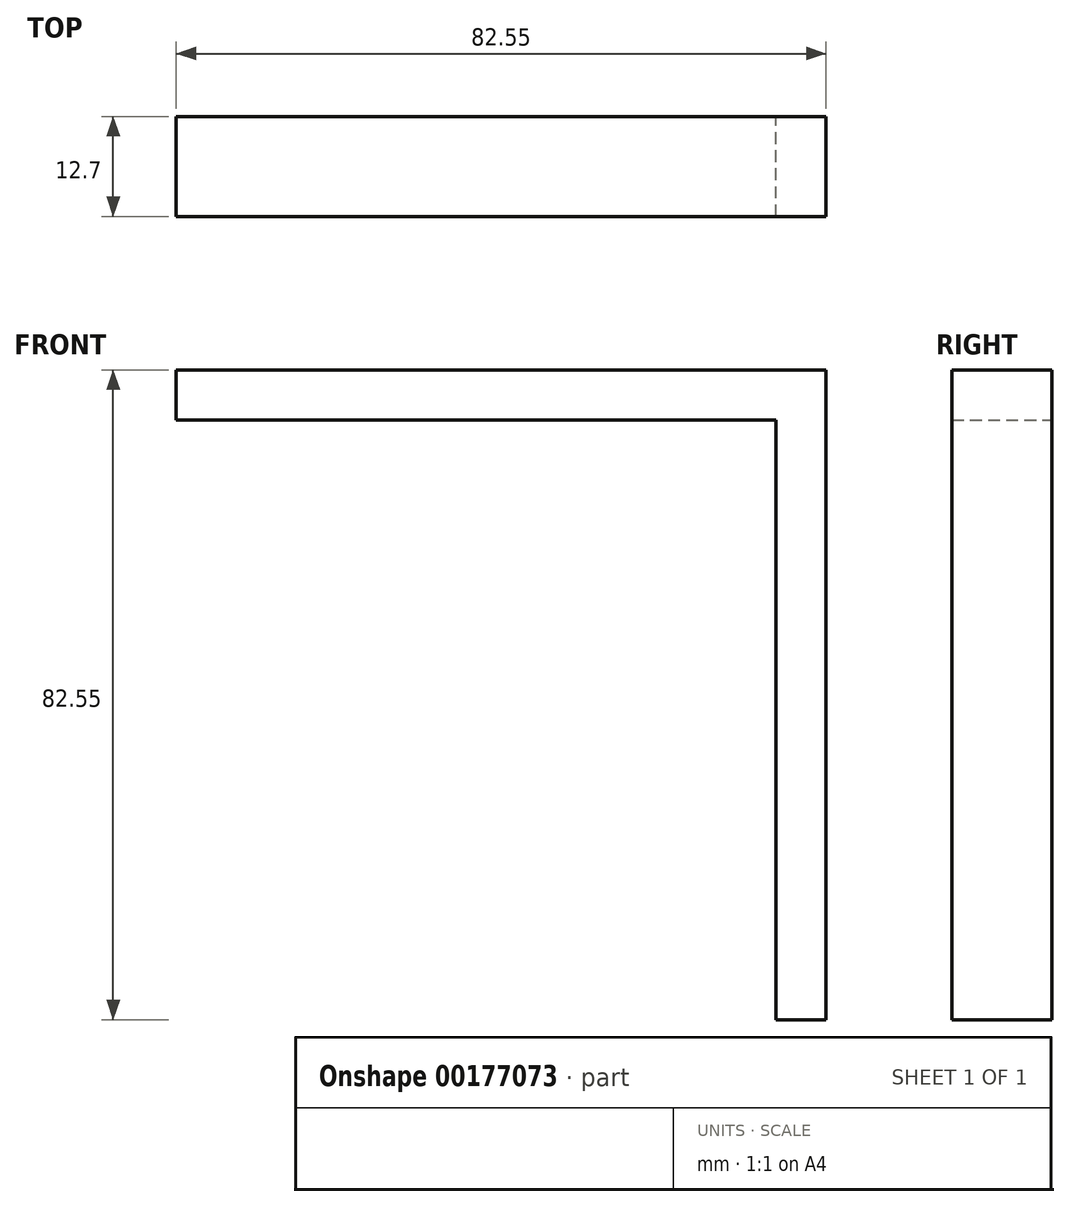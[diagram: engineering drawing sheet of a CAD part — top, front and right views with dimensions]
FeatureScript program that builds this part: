
annotation { "Feature Type Name" : "Feature", "Feature Type Description" : "" }
export const myFeature = defineFeature(function(context is Context, id is Id, definition is map)
    precondition{}
    {
        {
            var Q0;
            Q0=qCreatedBy(makeId("Front.planeOp"),FACE);
            var sketch = newSketch(context, id + "F0", { "sketchPlane" : qUnion([Q0])});
            skLineSegment(sketch, "E0", {"start": v(-15.66, 18.59) * mm, "end": v(-15.66, -57.61) * mm});
            skLineSegment(sketch, "E1", {"start": v(-15.66, 18.59) * mm, "end": v(-91.86, 18.59) * mm});
            skLineSegment(sketch, "E2.0", {"start": v(-15.66, 24.94) * mm, "end": v(-91.86, 24.94) * mm});
            skLineSegment(sketch, "E3.0", {"start": v(-9.3, 18.59) * mm, "end": v(-9.3, -57.61) * mm});
            skLineSegment(sketch, "E4", {"start": v(-15.66, 24.94) * mm, "end": v(-9.3, 24.94) * mm});
            skLineSegment(sketch, "E5", {"start": v(-9.3, 18.59) * mm, "end": v(-9.3, 24.94) * mm});
            skLineSegment(sketch, "E6", {"start": v(-91.86, 24.94) * mm, "end": v(-91.86, 18.59) * mm});
            skLineSegment(sketch, "E7", {"start": v(-15.66, -57.61) * mm, "end": v(-9.3, -57.61) * mm});
            skSolve(sketch);
        }
        {
            var Q0;
            Q0=makeQuery(id+"F0.imprint","IMPRINT",FACE,{"disambiguationData":[TD([[makeQuery(id+"F0.imprint","IMPRINT",EDGE,{"derivedFrom":sQuery(id+"F0.wireOp",EDGE,"E0")}),1.0]])]});
            extrude(context, id + "F1", {"entities" : qUnion([Q0]), "depth" : 12.7 * mm, "symmetric" : true});
        }
    });
